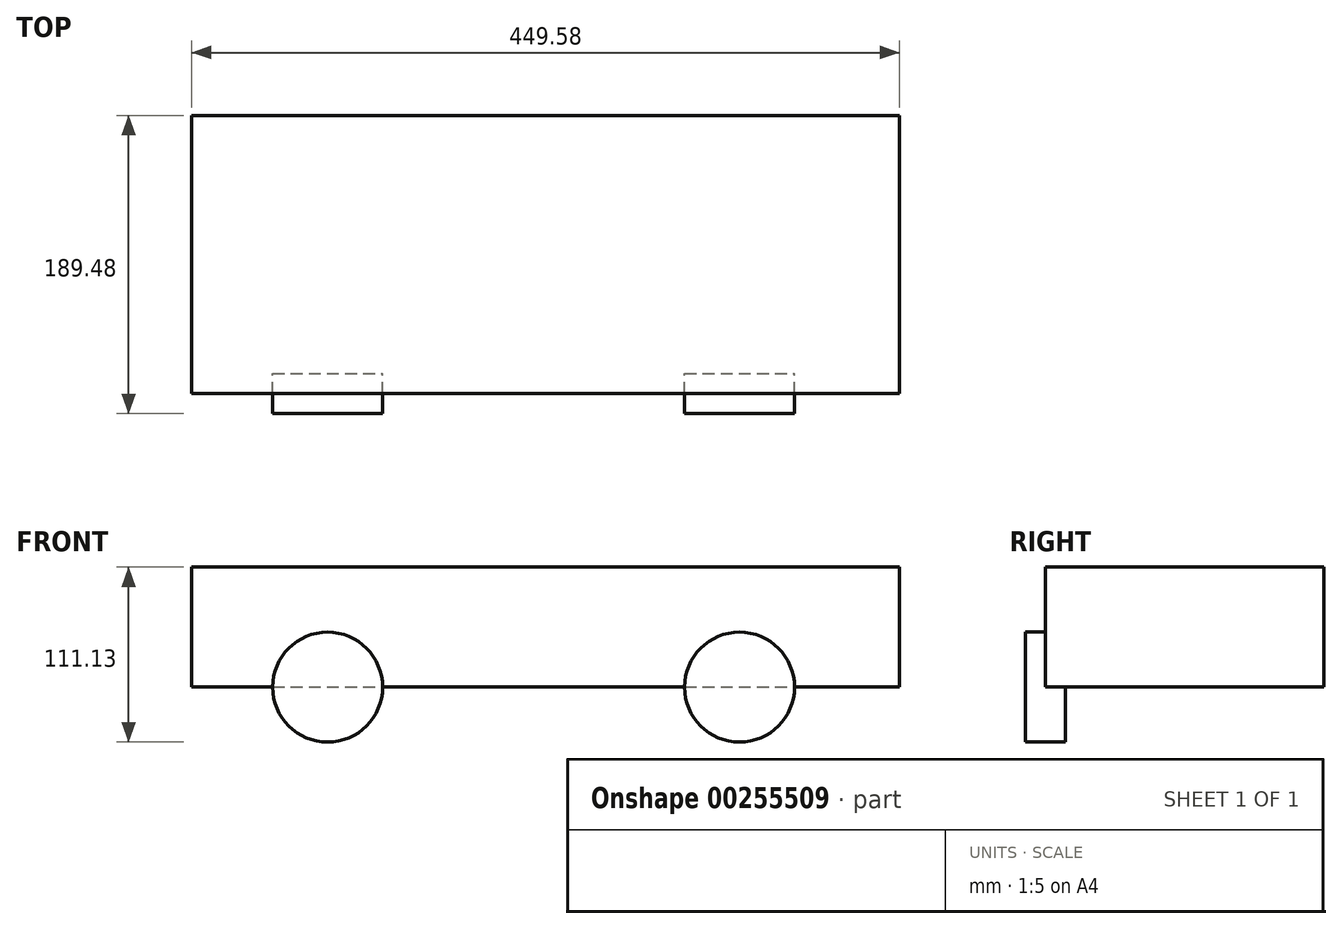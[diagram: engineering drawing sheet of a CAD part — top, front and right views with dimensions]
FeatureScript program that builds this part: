
annotation { "Feature Type Name" : "Feature", "Feature Type Description" : "" }
export const myFeature = defineFeature(function(context is Context, id is Id, definition is map)
    precondition{}
    {
        {
            var Q0;
            Q0=qCreatedBy(makeId("Top.planeOp"),FACE);
            var sketch = newSketch(context, id + "F0", { "sketchPlane" : qUnion([Q0])});
            skLineSegment(sketch, "E0.bottom", {"start": v(-225.86, 81.52) * mm, "end": v(223.72, 81.52) * mm});
            skLineSegment(sketch, "E0.top", {"start": v(-225.86, -95.26) * mm, "end": v(223.72, -95.26) * mm});
            skLineSegment(sketch, "E0.left", {"start": v(-225.86, 81.52) * mm, "end": v(-225.86, -95.26) * mm});
            skLineSegment(sketch, "E0.right", {"start": v(223.72, 81.52) * mm, "end": v(223.72, -95.26) * mm});
            skSolve(sketch);
        }
        {
            var Q0;
            Q0=makeQuery(id+"F0.imprint","IMPRINT",FACE,{"disambiguationData":[TD([[makeQuery(id+"F0.imprint","IMPRINT",EDGE,{"derivedFrom":sQuery(id+"F0.wireOp",EDGE,"E0.bottom")}),-1.0]])]});
            extrude(context, id + "F1", {"entities" : qUnion([Q0]), "depth" : 76.2 * mm});
        }
        {
            var Q0;
            Q0=makeQuery(id+"F1.opExtrude","SWEPT_FACE",FACE,{"disambiguationData":[OSD([sQuery(id+"F0.wireOp",EDGE,"E0.top")])]});
            var sketch = newSketch(context, id + "F2", { "sketchPlane" : qUnion([Q0])});
            skCircle(sketch, "E1", {"center": v(-139.5, 0) * mm, "radius": 34.93 * mm});
            skCircle(sketch, "E2", {"center": v(122.12, 0) * mm, "radius": 34.93 * mm});
            skSolve(sketch);
        }
        {
            var Q0;
            Q0 = qSketchRegion(id + "F2", true);
            extrude(context, id + "F3", {"entities" : qUnion([Q0]), "operationType" : NewBodyOperationType.ADD, "endBound" : BoundingType.SYMMETRIC, "depth" : 25.4 * mm});
        }
    });
